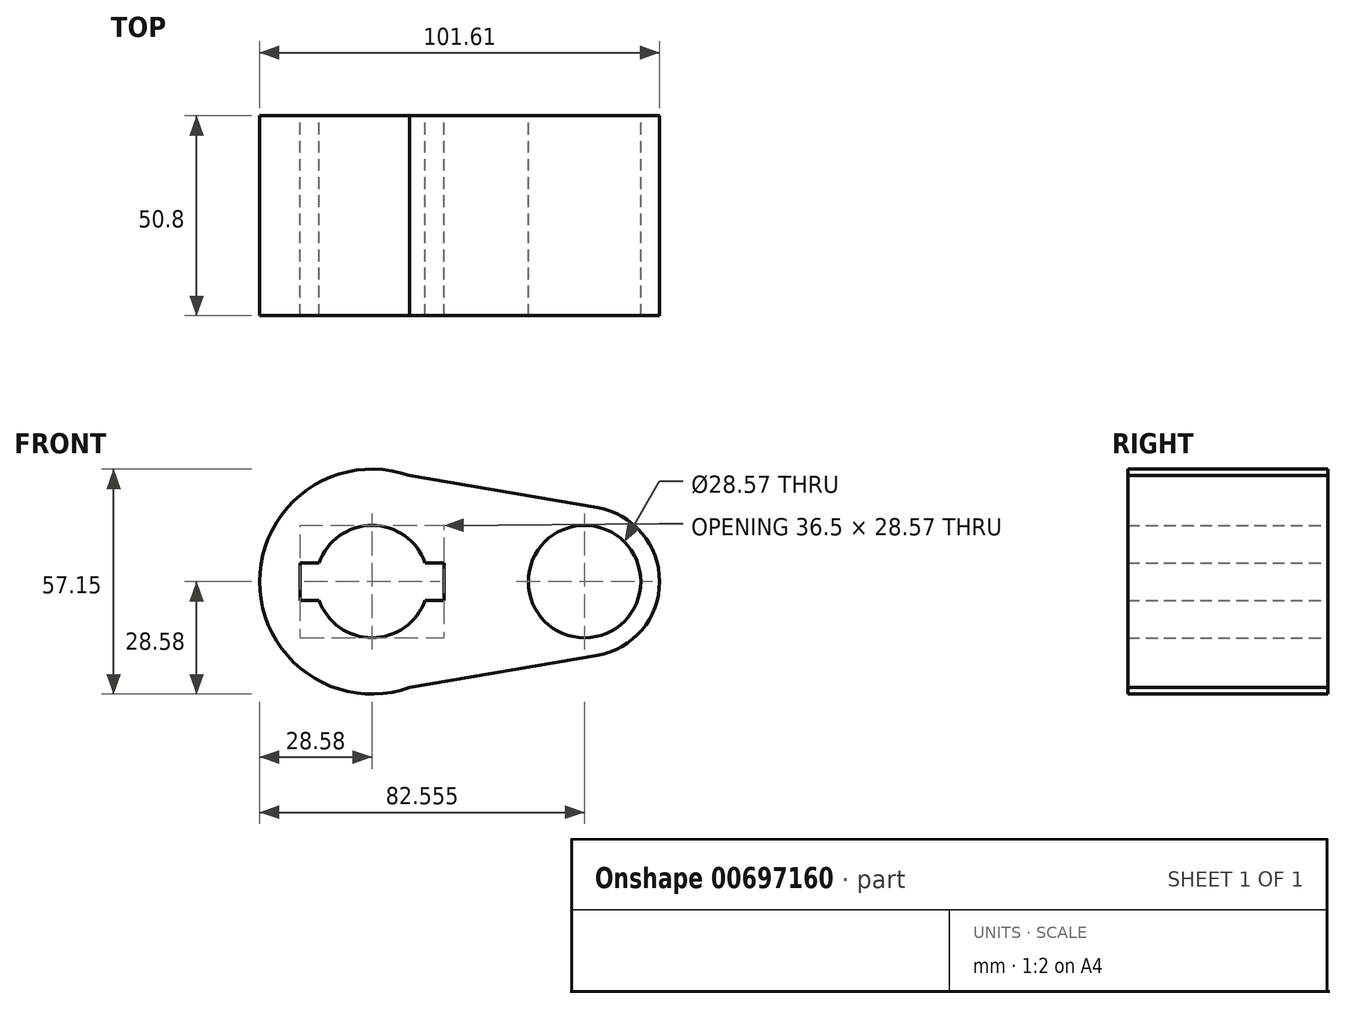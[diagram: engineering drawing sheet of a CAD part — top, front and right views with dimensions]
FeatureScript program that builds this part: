
annotation { "Feature Type Name" : "Feature", "Feature Type Description" : "" }
export const myFeature = defineFeature(function(context is Context, id is Id, definition is map)
    precondition{}
    {
        {
            var Q0;
            Q0=qCreatedBy(makeId("Front.planeOp"),FACE);
            var sketch = newSketch(context, id + "F0", { "sketchPlane" : qUnion([Q0])});
            skCircle(sketch, "E0", {"center": v(0, 0) * mm, "radius": 28.57 * mm});
            skCircle(sketch, "E1", {"center": v(53.98, 0) * mm, "radius": 19.05 * mm});
            skLineSegment(sketch, "E2", {"start": v(0, 28.58) * mm, "end": v(57.2, 18.78) * mm});
            skLineSegment(sketch, "E3", {"start": v(0, -28.58) * mm, "end": v(57.2, -18.78) * mm});
            skCircle(sketch, "E4", {"center": v(0, 0) * mm, "radius": 14.29 * mm});
            skCircle(sketch, "E5", {"center": v(53.98, 0) * mm, "radius": 14.29 * mm});
            skLineSegment(sketch, "E6.bottom", {"start": v(-18.25, -4.76) * mm, "end": v(18.25, -4.76) * mm});
            skLineSegment(sketch, "E6.top", {"start": v(-18.25, 4.76) * mm, "end": v(18.25, 4.76) * mm});
            skLineSegment(sketch, "E6.left", {"start": v(-18.25, -4.76) * mm, "end": v(-18.25, 4.76) * mm});
            skLineSegment(sketch, "E6.right", {"start": v(18.25, -4.76) * mm, "end": v(18.25, 4.76) * mm});
            skSolve(sketch);
        }
        {
            var Q0;
            Q0 = qSketchRegion(id + "F0", true);
            extrude(context, id + "F1", {"entities" : qUnion([Q0]), "depth" : 50.8 * mm, "offsetDistance" : 25.4 * mm});
        }
    });
